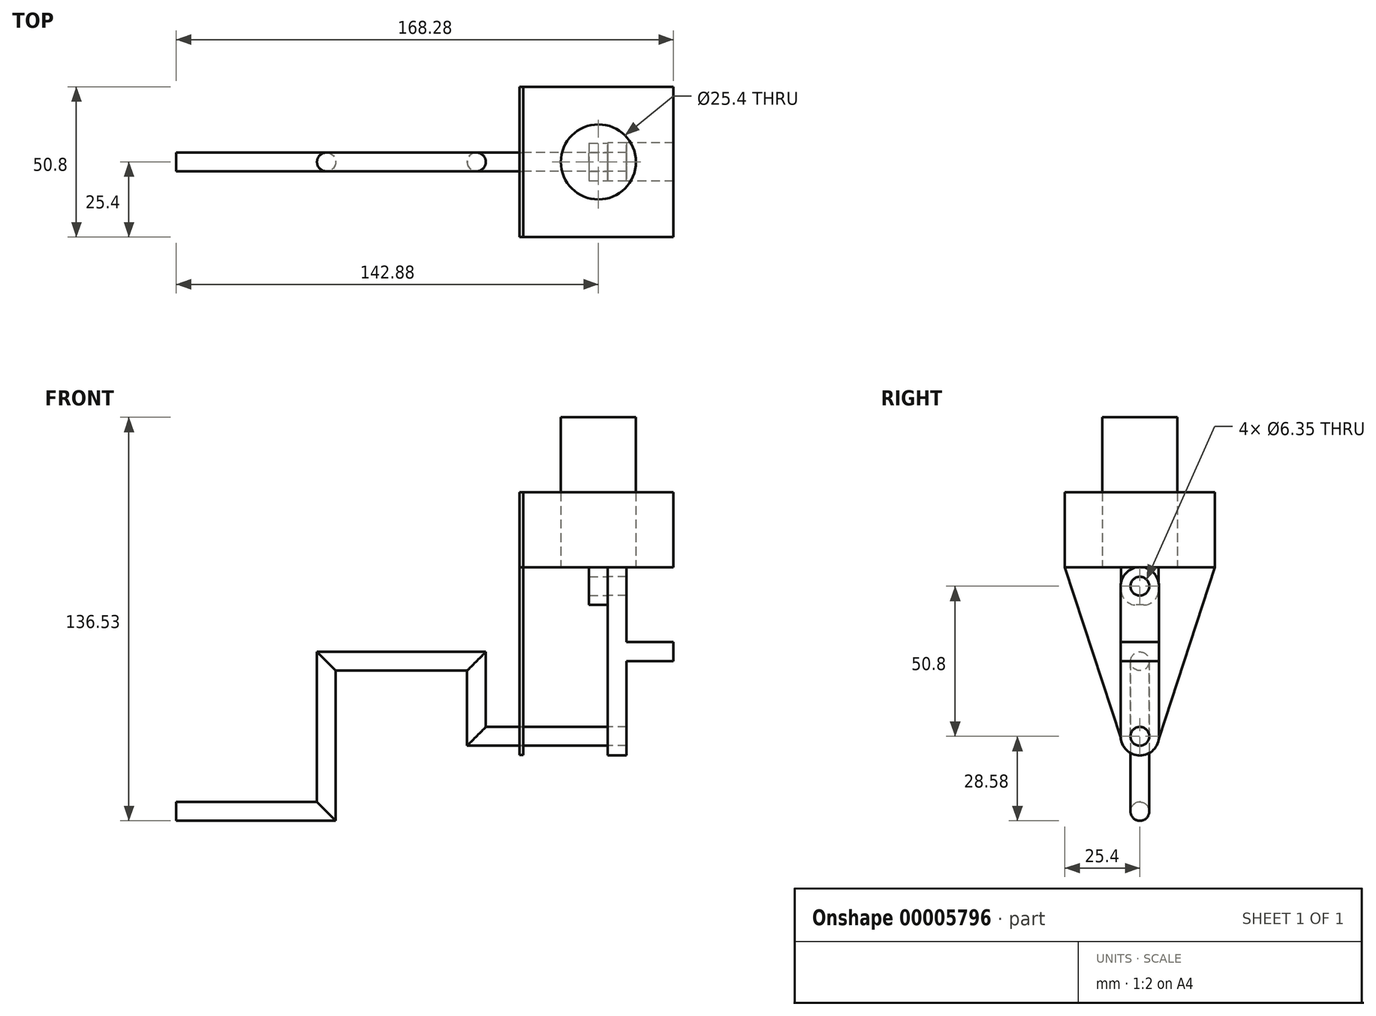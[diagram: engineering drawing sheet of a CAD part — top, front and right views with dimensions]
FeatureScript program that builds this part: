
annotation { "Feature Type Name" : "Feature", "Feature Type Description" : "" }
export const myFeature = defineFeature(function(context is Context, id is Id, definition is map)
    precondition{}
    {
        {
            var Q0;
            Q0=qCreatedBy(makeId("Top.planeOp"),FACE);
            var sketch = newSketch(context, id + "F0", { "sketchPlane" : qUnion([Q0])});
            skCircle(sketch, "E0", {"center": v(0, 0) * mm, "radius": 12.7 * mm});
            skSolve(sketch);
        }
        {
            var Q0;
            Q0=makeQuery(id+"F0.imprint","IMPRINT",FACE,{"disambiguationData":[TD([[makeQuery(id+"F0.imprint","IMPRINT",EDGE,{"derivedFrom":sQuery(id+"F0.wireOp",EDGE,"E0")}),1.0]])]});
            var Q1;
            Q1=sQuery(id+"F0.wireOp",EDGE,"E0");
            extrude(context, id + "F1", {"entities" : qUnion([Q0]), "surfaceEntities" : qUnion([Q1]), "depth" : 50.8 * mm});
        }
        {
            var Q0;
            Q0=makeQuery(id+"F1.opExtrude","CAP_FACE",FACE,{"disambiguationData":[OSD([sQuery(id+"F0.wireOp",EDGE,"E0")])],"isStart":true});
            var sketch = newSketch(context, id + "F2", { "sketchPlane" : qUnion([Q0])});
            skLineSegment(sketch, "E1.rect.bottom", {"start": v(-3.17, -6.35) * mm, "end": v(3.18, -6.35) * mm});
            skLineSegment(sketch, "E1.rect.top", {"start": v(-3.18, 6.35) * mm, "end": v(3.17, 6.35) * mm});
            skLineSegment(sketch, "E1.rect.left", {"start": v(-3.17, -6.35) * mm, "end": v(-3.18, 6.35) * mm});
            skLineSegment(sketch, "E1.rect.right", {"start": v(3.18, -6.35) * mm, "end": v(3.17, 6.35) * mm});
            skPoint(sketch, "E1.rect.middle", {"position": v(0, 0) * mm});
            skSolve(sketch);
        }
        {
            var Q0;
            Q0=makeQuery(id+"F2.imprint","IMPRINT",FACE,{"disambiguationData":[TD([[makeQuery(id+"F2.imprint","IMPRINT",EDGE,{"derivedFrom":sQuery(id+"F2.wireOp",EDGE,"E1.rect.bottom")}),1.0]])]});
            extrude(context, id + "F3", {"entities" : qUnion([Q0]), "operationType" : NewBodyOperationType.ADD, "depth" : 12.7 * mm});
        }
        {
            var Q0;
            Q0=makeQuery(id+"F3.opExtrude","SWEPT_FACE",FACE,{"disambiguationData":[OSD([sQuery(id+"F2.wireOp",EDGE,"E1.rect.right")])]});
            var sketch = newSketch(context, id + "F4", { "sketchPlane" : qUnion([Q0])});
            skCircle(sketch, "E2", {"center": v(0, -6.35) * mm, "radius": 3.17 * mm});
            skSolve(sketch);
        }
        {
            var Q0;
            Q0=makeQuery(id+"F4.imprint","IMPRINT",FACE,{"disambiguationData":[TD([[makeQuery(id+"F4.imprint","IMPRINT",EDGE,{"derivedFrom":sQuery(id+"F4.wireOp",EDGE,"E2")}),1.0]])]});
            var Q1;
            Q1=sQuery(id+"F4.wireOp",EDGE,"E2");
            extrude(context, id + "F5", {"entities" : qUnion([Q0]), "operationType" : NewBodyOperationType.REMOVE, "surfaceEntities" : qUnion([Q1]), "oppositeDirection" : true, "depth" : 25.4 * mm});
        }
        {
            var Q0;
            Q0=makeQuery(id+"F3.opExtrude","CAP_EDGE",EDGE,{"disambiguationData":[OSD([sQuery(id+"F2.wireOp",EDGE,"E1.rect.bottom")])],"isStart":false});
            var Q1;
            Q1=makeQuery(id+"F3.opExtrude","CAP_EDGE",EDGE,{"disambiguationData":[OSD([sQuery(id+"F2.wireOp",EDGE,"E1.rect.top")])],"isStart":false});
            fillet(context, id + "F6", {"entities" : qUnion([Q0, Q1]), "radius" : 5.08 * mm, "tangentPropagation" : true, "allowEdgeOverflow" : false});
        }
        {
            var Q0;
            Q0=qCreatedBy(makeId("Top.planeOp"),FACE);
            var sketch = newSketch(context, id + "F7", { "sketchPlane" : qUnion([Q0])});
            skLineSegment(sketch, "E3.rect.bottom", {"start": v(25.4, 25.4) * mm, "end": v(-25.4, 25.4) * mm});
            skLineSegment(sketch, "E3.rect.top", {"start": v(25.4, -25.4) * mm, "end": v(-25.4, -25.4) * mm});
            skLineSegment(sketch, "E3.rect.left", {"start": v(25.4, 25.4) * mm, "end": v(25.4, -25.4) * mm});
            skLineSegment(sketch, "E3.rect.right", {"start": v(-25.4, 25.4) * mm, "end": v(-25.4, -25.4) * mm});
            skPoint(sketch, "E3.rect.middle", {"position": v(0, 0) * mm});
            skSolve(sketch);
        }
        {
            var Q0;
            Q0=makeQuery(id+"F7.imprint","IMPRINT",FACE,{"disambiguationData":[TD([[makeQuery(id+"F7.imprint","IMPRINT",EDGE,{"derivedFrom":sQuery(id+"F7.wireOp",EDGE,"E3.rect.bottom")}),1.0]])]});
            extrude(context, id + "F8", {"entities" : qUnion([Q0]), "depth" : 25.4 * mm});
        }
        {
            var Q0;
            Q0=makeQuery(id+"F1.opExtrude","SWEPT_BODY",BODY,{"disambiguationData":[OSD([sQuery(id+"F0.wireOp",EDGE,"E0")])]});
            var Q1;
            Q1=makeQuery(id+"F8.opExtrude","SWEPT_BODY",BODY,{"disambiguationData":[OSD([sQuery(id+"F7.wireOp",EDGE,"E3.rect.bottom"),sQuery(id+"F7.wireOp",EDGE,"E3.rect.top"),sQuery(id+"F7.wireOp",EDGE,"E3.rect.left"),sQuery(id+"F7.wireOp",EDGE,"E3.rect.right")])]});
            booleanBodies(context, id + "F9", {"operationType" : BooleanOperationType.SUBTRACTION, "tools" : qUnion([Q0]), "targets" : qUnion([Q1]), "keepTools" : true});
        }
        {
            var Q0;
            Q0=makeQuery(id+"F3.opExtrude","SWEPT_FACE",FACE,{"disambiguationData":[OSD([sQuery(id+"F2.wireOp",EDGE,"E1.rect.right")])]});
            var sketch = newSketch(context, id + "F10", { "sketchPlane" : qUnion([Q0])});
            skCircle(sketch, "E4.0", {"center": v(0, -6.35) * mm, "radius": 3.17 * mm});
            skArc(sketch, "E5", {"start": v(6.48, -6.35) * mm, "mid": v(0, 0.13) * mm, "end": v(-6.48, -6.35) * mm});
            skLineSegment(sketch, "E6", {"start": v(6.48, -6.35) * mm, "end": v(6.48, -57.15) * mm});
            skLineSegment(sketch, "E7", {"start": v(-6.48, -6.35) * mm, "end": v(-6.48, -57.15) * mm});
            skArc(sketch, "E8", {"start": v(-6.48, -57.15) * mm, "mid": v(0, -63.63) * mm, "end": v(6.48, -57.15) * mm});
            skCircle(sketch, "E9", {"center": v(0, -57.15) * mm, "radius": 3.18 * mm});
            skSolve(sketch);
        }
        {
            var Q0;
            Q0 = qSketchRegion(id + "F10", true);
            extrude(context, id + "F11", {"entities" : qUnion([Q0]), "depth" : 6.35 * mm});
        }
        {
            var Q0;
            Q0=makeQuery(id+"F11.opExtrude","CAP_FACE",FACE,{"disambiguationData":[OSD([sQuery(id+"F10.wireOp",EDGE,"E4.0"),sQuery(id+"F10.wireOp",EDGE,"E5"),sQuery(id+"F10.wireOp",EDGE,"E6"),sQuery(id+"F10.wireOp",EDGE,"E7"),sQuery(id+"F10.wireOp",EDGE,"E8"),sQuery(id+"F10.wireOp",EDGE,"E9")])],"isStart":false});
            var sketch = newSketch(context, id + "F12", { "sketchPlane" : qUnion([Q0])});
            skCircle(sketch, "E10.0", {"center": v(0, -57.15) * mm, "radius": 3.18 * mm});
            skSolve(sketch);
        }
        {
            var Q0;
            Q0=qCreatedBy(makeId("Front.planeOp"),FACE);
            var sketch = newSketch(context, id + "F13", { "sketchPlane" : qUnion([Q0])});
            skPoint(sketch, "E11.0", {"position": v(9.53, -57.15) * mm});
            skLineSegment(sketch, "E12", {"start": v(9.52, -57.15) * mm, "end": v(-41.27, -57.15) * mm});
            skLineSegment(sketch, "E13", {"start": v(-41.27, -57.15) * mm, "end": v(-41.27, -31.75) * mm});
            skLineSegment(sketch, "E14", {"start": v(-41.28, -31.75) * mm, "end": v(-92.08, -31.75) * mm});
            skLineSegment(sketch, "E15", {"start": v(-92.08, -31.75) * mm, "end": v(-92.08, -82.55) * mm});
            skLineSegment(sketch, "E16", {"start": v(-92.08, -82.55) * mm, "end": v(-142.88, -82.55) * mm});
            skSolve(sketch);
        }
        {
            var Q0;
            Q0 = qSketchRegion(id + "F12", true);
            var Q1;
            Q1 = qBodyType(qCreatedBy(id + "F13" ,EDGE), BodyType.WIRE);
            sweep(context, id + "F14", {"profiles" : qUnion([Q0]), "path" : qUnion([Q1])});
        }
        {
            var Q0;
            Q0=makeQuery(id+"F11.opExtrude","CAP_FACE",FACE,{"disambiguationData":[OSD([sQuery(id+"F10.wireOp",EDGE,"E4.0"),sQuery(id+"F10.wireOp",EDGE,"E5"),sQuery(id+"F10.wireOp",EDGE,"E6"),sQuery(id+"F10.wireOp",EDGE,"E7"),sQuery(id+"F10.wireOp",EDGE,"E8"),sQuery(id+"F10.wireOp",EDGE,"E9")])],"isStart":false});
            var sketch = newSketch(context, id + "F15", { "sketchPlane" : qUnion([Q0])});
            skLineSegment(sketch, "E17.rect.bottom", {"start": v(6.48, -31.75) * mm, "end": v(-6.48, -31.75) * mm});
            skLineSegment(sketch, "E17.rect.top", {"start": v(6.48, -25.27) * mm, "end": v(-6.48, -25.27) * mm});
            skLineSegment(sketch, "E17.rect.left", {"start": v(6.48, -31.75) * mm, "end": v(6.48, -25.27) * mm});
            skLineSegment(sketch, "E17.rect.right", {"start": v(-6.48, -31.75) * mm, "end": v(-6.48, -25.27) * mm});
            skPoint(sketch, "E17.rect.middle", {"position": v(0, -28.51) * mm});
            skSolve(sketch);
        }
        {
            var Q0;
            Q0=makeQuery(id+"F15.imprint","IMPRINT",FACE,{"disambiguationData":[TD([[makeQuery(id+"F15.imprint","IMPRINT",EDGE,{"derivedFrom":sQuery(id+"F15.wireOp",EDGE,"E17.rect.bottom")}),-1.0]])]});
            var Q1;
            Q1=makeQuery(id+"F8.opExtrude","SWEPT_FACE",FACE,{"disambiguationData":[OSD([sQuery(id+"F7.wireOp",EDGE,"E3.rect.left")])]});
            extrude(context, id + "F16", {"entities" : qUnion([Q0]), "operationType" : NewBodyOperationType.ADD, "endBound" : BoundingType.UP_TO_SURFACE, "endBoundEntityFace" : qUnion([Q1]), "depth" : 25.4 * mm});
        }
        {
            var Q0;
            Q0=makeQuery(id+"F8.opExtrude","SWEPT_FACE",FACE,{"disambiguationData":[OSD([sQuery(id+"F7.wireOp",EDGE,"E3.rect.right")])]});
            var sketch = newSketch(context, id + "F17", { "sketchPlane" : qUnion([Q0])});
            skLineSegment(sketch, "E18.0.1", {"start": v(25.4, 0) * mm, "end": v(25.4, 25.4) * mm});
            skLineSegment(sketch, "E18.0.2", {"start": v(25.4, 25.4) * mm, "end": v(-25.4, 25.4) * mm});
            skLineSegment(sketch, "E18.0.3", {"start": v(-25.4, 25.4) * mm, "end": v(-25.4, 0) * mm});
            skCircle(sketch, "E19.0", {"center": v(0, -57.15) * mm, "radius": 3.18 * mm});
            skArc(sketch, "E20", {"start": v(-6.03, -59.13) * mm, "mid": v(0, -63.5) * mm, "end": v(6.03, -59.13) * mm});
            skLineSegment(sketch, "E21", {"start": v(-25.4, 0) * mm, "end": v(-6.03, -59.13) * mm});
            skLineSegment(sketch, "E22", {"start": v(25.4, 0) * mm, "end": v(6.03, -59.13) * mm});
            skSolve(sketch);
        }
        {
            var Q0;
            Q0 = qSketchRegion(id + "F17", true);
            extrude(context, id + "F18", {"entities" : qUnion([Q0]), "depth" : 1.27 * mm});
        }
    });
